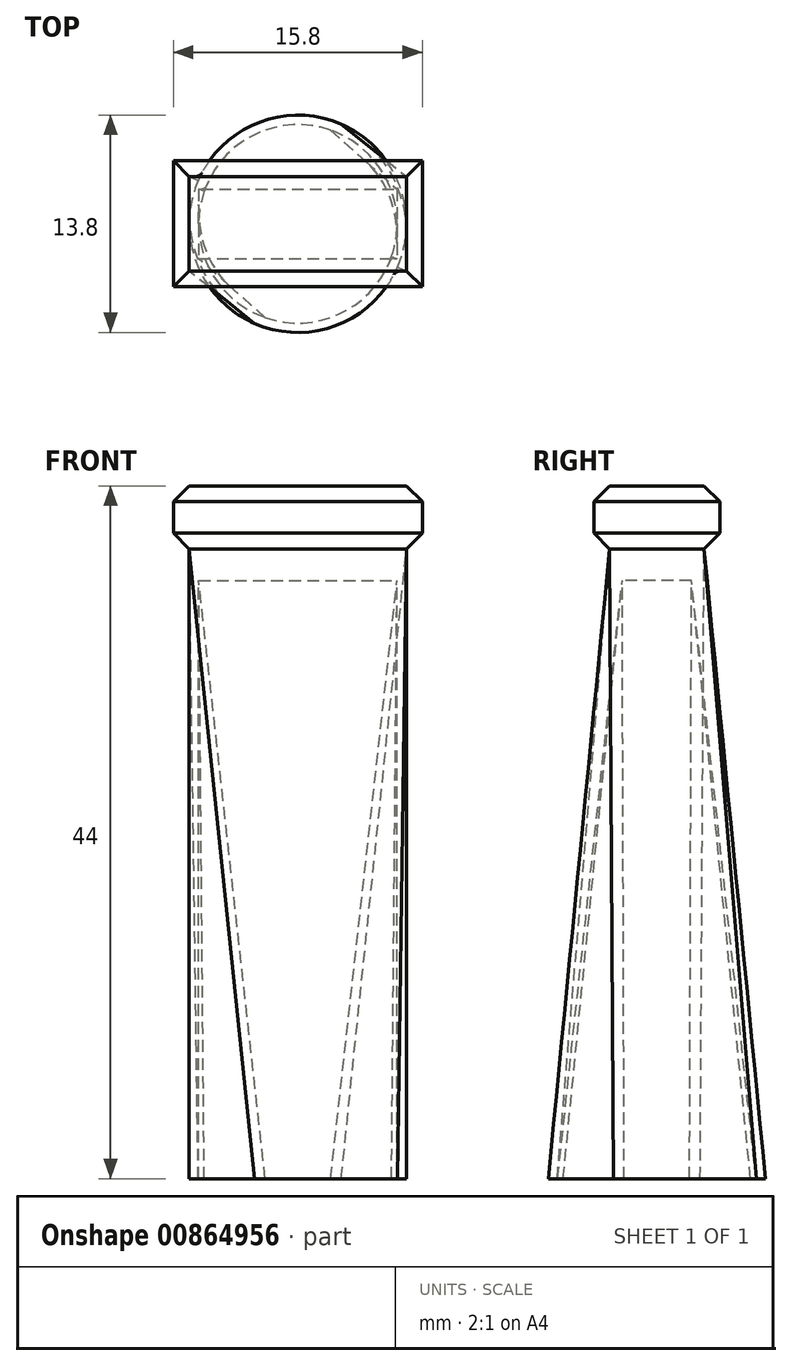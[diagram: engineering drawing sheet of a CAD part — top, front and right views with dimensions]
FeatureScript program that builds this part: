
annotation { "Feature Type Name" : "Feature", "Feature Type Description" : "" }
export const myFeature = defineFeature(function(context is Context, id is Id, definition is map)
    precondition{}
    {
        {
            var Q0;
            Q0=qCreatedBy(makeId("Top.planeOp"),FACE);
            var sketch = newSketch(context, id + "F0", { "sketchPlane" : qUnion([Q0])});
            skCircle(sketch, "E0", {"center": v(0, 0) * mm, "radius": 6.9 * mm});
            skSolve(sketch);
        }
        {
            var Q0;
            Q0=qCreatedBy(makeId("Top.planeOp"),FACE);
            cPlane(context, id + "F1", {"entities" : qUnion([Q0]), "cplaneType" : CPlaneType.OFFSET, "offset" : 40 * mm, "width" : 150 * mm, "height" : 150 * mm});
        }
        {
            var Q0;
            Q0=qCreatedBy(id+"F1.planeOp",FACE);
            var sketch = newSketch(context, id + "F2", { "sketchPlane" : qUnion([Q0])});
            skLineSegment(sketch, "E1.bottom", {"start": v(-6.9, 3) * mm, "end": v(6.9, 3) * mm});
            skLineSegment(sketch, "E1.top", {"start": v(-6.9, -3) * mm, "end": v(6.9, -3) * mm});
            skLineSegment(sketch, "E1.left", {"start": v(-6.9, 3) * mm, "end": v(-6.9, -3) * mm});
            skLineSegment(sketch, "E1.right", {"start": v(6.9, 3) * mm, "end": v(6.9, -3) * mm});
            skPoint(sketch, "E1.middle", {"position": v(0, 0) * mm});
            skSolve(sketch);
        }
        {
            var Q0;
            Q0=makeQuery(id+"F0.imprint","IMPRINT",FACE,{"disambiguationData":[TD([[makeQuery(id+"F0.imprint","IMPRINT",EDGE,{"derivedFrom":sQuery(id+"F0.wireOp",EDGE,"E0")}),1.0]])]});
            var Q1;
            Q1=makeQuery(id+"F2.imprint","IMPRINT",FACE,{"disambiguationData":[TD([[makeQuery(id+"F2.imprint","IMPRINT",EDGE,{"derivedFrom":sQuery(id+"F2.wireOp",EDGE,"E1.bottom")}),-1.0]])]});
            loft(context, id + "F3", {"sheetProfilesArray" : [{ "sheetProfileEntities" : qUnion([Q0]) }, { "sheetProfileEntities" : qUnion([Q1]) }]});
        }
        {
            var Q0;
            Q0=qCreatedBy(makeId("Top.planeOp"),FACE);
            cPlane(context, id + "F4", {"entities" : qUnion([Q0]), "cplaneType" : CPlaneType.OFFSET, "offset" : 38 * mm, "width" : 150 * mm, "height" : 150 * mm});
        }
        {
            var Q0;
            Q0=qCreatedBy(makeId("Top.planeOp"),FACE);
            var sketch = newSketch(context, id + "F5", { "sketchPlane" : qUnion([Q0])});
            skCircle(sketch, "E2", {"center": v(0, 0) * mm, "radius": 6.3 * mm});
            skSolve(sketch);
        }
        {
            var Q0;
            Q0=qCreatedBy(id+"F4.planeOp",FACE);
            var sketch = newSketch(context, id + "F6", { "sketchPlane" : qUnion([Q0])});
            skLineSegment(sketch, "E3.bottom", {"start": v(-6.3, 2.2) * mm, "end": v(6.3, 2.2) * mm});
            skLineSegment(sketch, "E3.top", {"start": v(-6.3, -2.2) * mm, "end": v(6.3, -2.2) * mm});
            skLineSegment(sketch, "E3.left", {"start": v(-6.3, 2.2) * mm, "end": v(-6.3, -2.2) * mm});
            skLineSegment(sketch, "E3.right", {"start": v(6.3, 2.2) * mm, "end": v(6.3, -2.2) * mm});
            skPoint(sketch, "E3.middle", {"position": v(0, 0) * mm});
            skSolve(sketch);
        }
        {
            var Q1;
            Q1 = qSketchRegion(id + "F5", true);
            var Q2;
            Q2 = qSketchRegion(id + "F6", true);
            loft(context, id + "F7", {"operationType" : NewBodyOperationType.REMOVE, "sheetProfilesArray" : [{ "sheetProfileEntities" : qUnion([Q1]) }, { "sheetProfileEntities" : qUnion([Q2]) }]});
        }
        {
            var Q0;
            Q0=qCreatedBy(id+"F1.planeOp",FACE);
            var sketch = newSketch(context, id + "F8", { "sketchPlane" : qUnion([Q0])});
            skLineSegment(sketch, "E4.bottom", {"start": v(7.9, 4) * mm, "end": v(-7.9, 4) * mm});
            skLineSegment(sketch, "E4.top", {"start": v(7.9, -4) * mm, "end": v(-7.9, -4) * mm});
            skLineSegment(sketch, "E4.left", {"start": v(7.9, 4) * mm, "end": v(7.9, -4) * mm});
            skLineSegment(sketch, "E4.right", {"start": v(-7.9, 4) * mm, "end": v(-7.9, -4) * mm});
            skPoint(sketch, "E4.middle", {"position": v(0, 0) * mm});
            skSolve(sketch);
        }
        {
            var Q0;
            Q0 = qSketchRegion(id + "F8", true);
            extrude(context, id + "F9", {"entities" : qUnion([Q0]), "operationType" : NewBodyOperationType.ADD, "depth" : 4 * mm, "offsetDistance" : 25 * mm});
        }
        {
            var Q0;
            Q0=makeQuery(id+"F9.opExtrude","CAP_EDGE",EDGE,{"disambiguationData":[OSD([sQuery(id+"F8.wireOp",EDGE,"E4.left")])],"isStart":false});
            var Q1;
            Q1=makeQuery(id+"F9.opExtrude","CAP_EDGE",EDGE,{"disambiguationData":[OSD([sQuery(id+"F8.wireOp",EDGE,"E4.top")])],"isStart":false});
            var Q2;
            Q2=makeQuery(id+"F9.opExtrude","CAP_EDGE",EDGE,{"disambiguationData":[OSD([sQuery(id+"F8.wireOp",EDGE,"E4.bottom")])],"isStart":false});
            var Q3;
            Q3=makeQuery(id+"F9.opExtrude","CAP_EDGE",EDGE,{"disambiguationData":[OSD([sQuery(id+"F8.wireOp",EDGE,"E4.right")])],"isStart":false});
            var Q4;
            Q4=makeQuery(id+"F9.opExtrude","CAP_EDGE",EDGE,{"disambiguationData":[OSD([sQuery(id+"F8.wireOp",EDGE,"E4.top")])],"isStart":true});
            var Q5;
            Q5=makeQuery(id+"F9.opExtrude","CAP_EDGE",EDGE,{"disambiguationData":[OSD([sQuery(id+"F8.wireOp",EDGE,"E4.right")])],"isStart":true});
            var Q6;
            Q6=makeQuery(id+"F9.opExtrude","CAP_EDGE",EDGE,{"disambiguationData":[OSD([sQuery(id+"F8.wireOp",EDGE,"E4.bottom")])],"isStart":true});
            var Q7;
            Q7=makeQuery(id+"F9.opExtrude","CAP_EDGE",EDGE,{"disambiguationData":[OSD([sQuery(id+"F8.wireOp",EDGE,"E4.left")])],"isStart":true});
            chamfer(context, id + "F10", {"entities" : qUnion([Q0, Q1, Q2, Q3, Q4, Q5, Q6, Q7]), "width" : 1 * mm, "tangentPropagation" : true});
        }
    });
